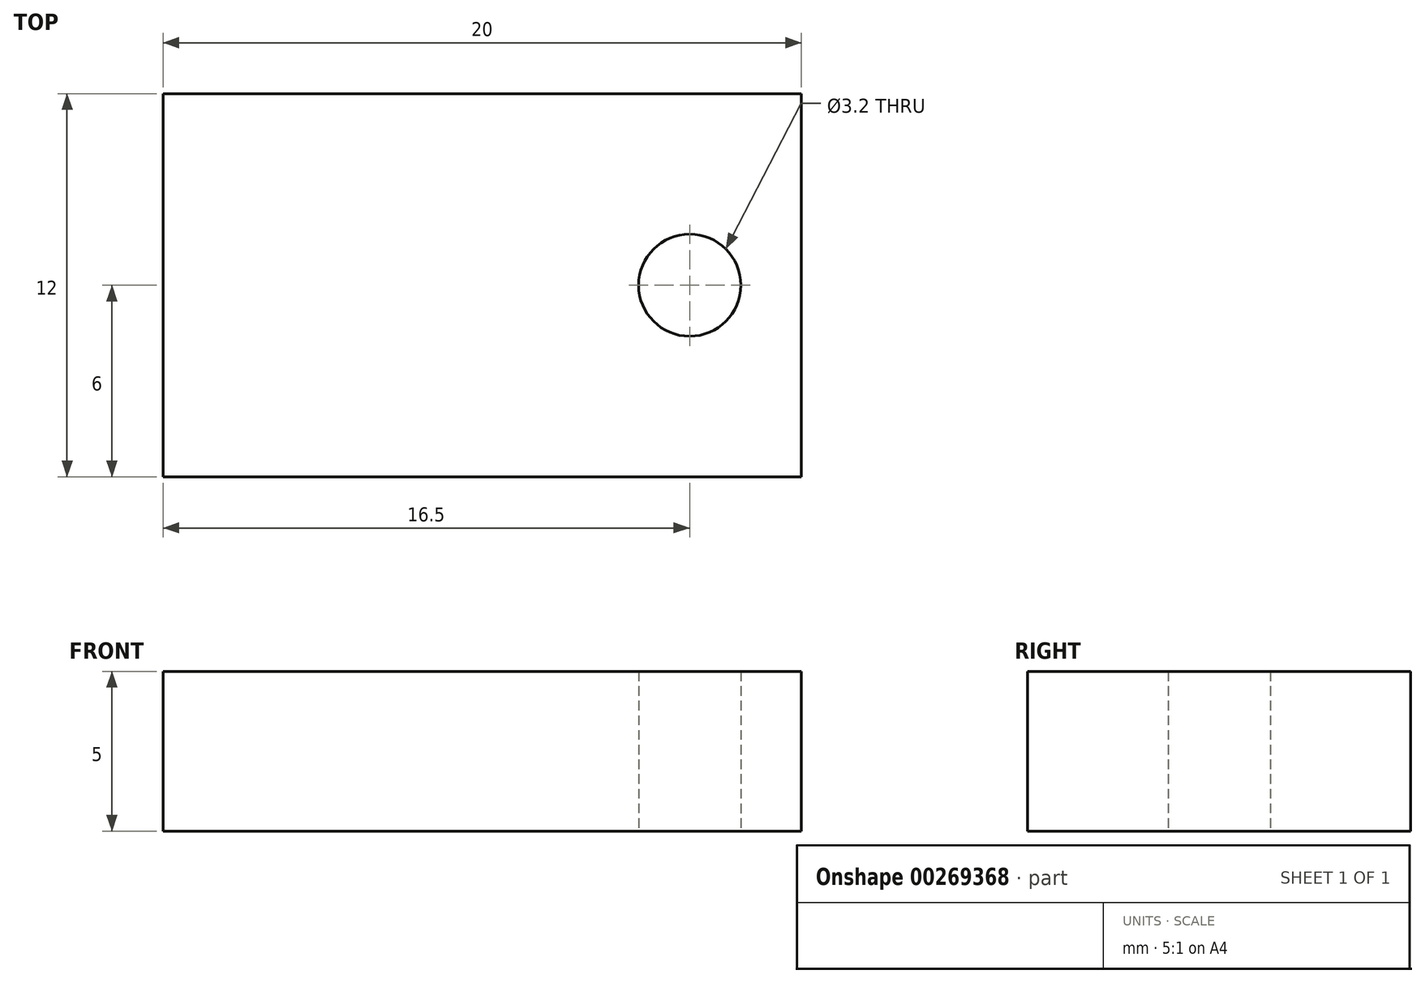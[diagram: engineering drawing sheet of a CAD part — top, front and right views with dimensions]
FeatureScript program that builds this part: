
annotation { "Feature Type Name" : "Feature", "Feature Type Description" : "" }
export const myFeature = defineFeature(function(context is Context, id is Id, definition is map)
    precondition{}
    {
        {
            var Q0;
            Q0=qCreatedBy(makeId("Top.planeOp"),FACE);
            var sketch = newSketch(context, id + "F0", { "sketchPlane" : qUnion([Q0])});
            skLineSegment(sketch, "E0.bottom", {"start": v(10, 6) * mm, "end": v(-10, 6) * mm});
            skLineSegment(sketch, "E0.top", {"start": v(10, -6) * mm, "end": v(-10, -6) * mm});
            skLineSegment(sketch, "E0.left", {"start": v(10, 6) * mm, "end": v(10, -6) * mm});
            skLineSegment(sketch, "E0.right", {"start": v(-10, 6) * mm, "end": v(-10, -6) * mm});
            skPoint(sketch, "E0.middle", {"position": v(0, 0) * mm});
            skLineSegment(sketch, "E1", {"start": v(10, 0) * mm, "end": v(6.5, 0) * mm});
            skPoint(sketch, "E1.endSnap0", {"position": v(10, 0) * mm});
            skCircle(sketch, "E2", {"center": v(6.5, 0) * mm, "radius": 1.6 * mm});
            skSolve(sketch);
        }
        {
            var Q0;
            Q0 = qSketchRegion(id + "F0", true);
            extrude(context, id + "F1", {"entities" : qUnion([Q0]), "depth" : 5 * mm});
        }
    });
